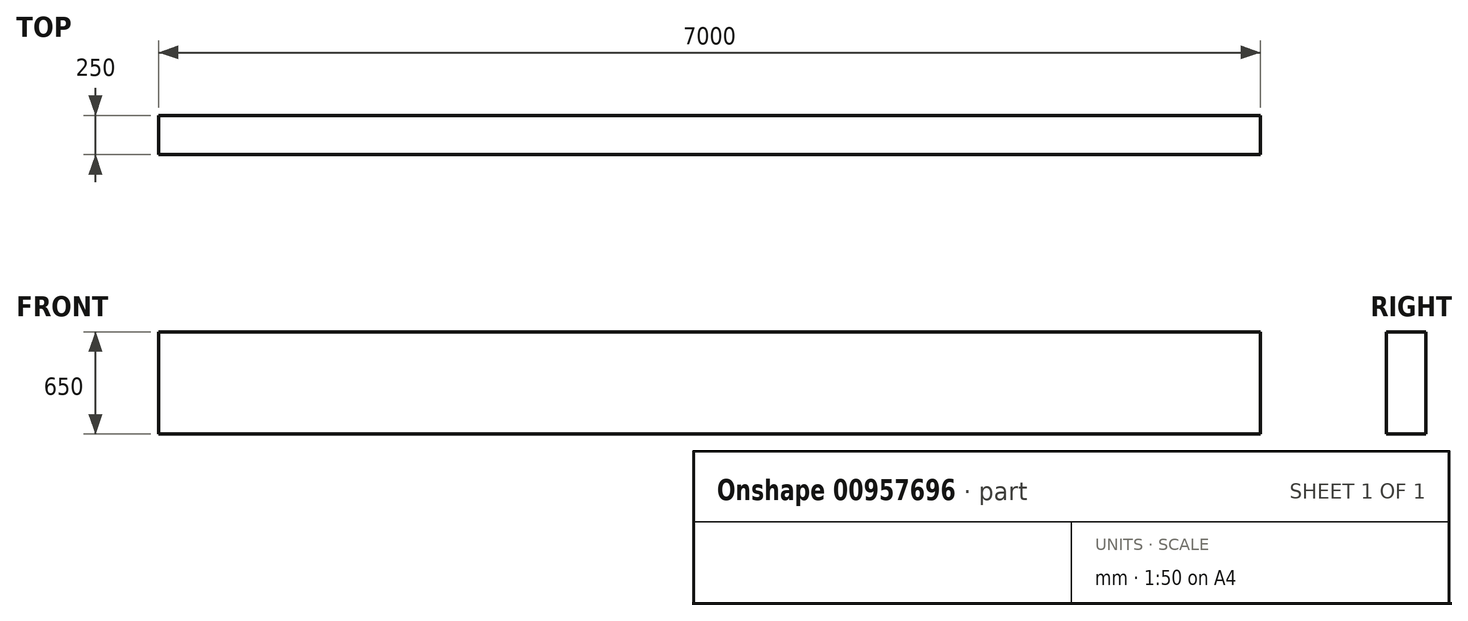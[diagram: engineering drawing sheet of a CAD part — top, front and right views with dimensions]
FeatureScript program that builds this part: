
annotation { "Feature Type Name" : "Feature", "Feature Type Description" : "" }
export const myFeature = defineFeature(function(context is Context, id is Id, definition is map)
    precondition{}
    {
        {
            var Q0;
            Q0=qCreatedBy(makeId("Front.planeOp"),FACE);
            var sketch = newSketch(context, id + "F0", { "sketchPlane" : qUnion([Q0])});
            skLineSegment(sketch, "E0", {"start": v(-3491.85, -4612.2) * mm, "end": v(3508.15, -4612.2) * mm});
            skLineSegment(sketch, "E1", {"start": v(3508.15, -4612.2) * mm, "end": v(3508.15, -5262.2) * mm});
            skLineSegment(sketch, "E2", {"start": v(3508.15, -5262.2) * mm, "end": v(-3491.85, -5262.2) * mm});
            skLineSegment(sketch, "E3", {"start": v(-3491.85, -5262.2) * mm, "end": v(-3491.85, -4612.2) * mm});
            skSolve(sketch);
        }
        {
            var Q0;
            Q0=makeQuery(id+"F0.imprint","IMPRINT",FACE,{"disambiguationData":[TD([[makeQuery(id+"F0.imprint","IMPRINT",EDGE,{"derivedFrom":sQuery(id+"F0.wireOp",EDGE,"E0")}),-1.0]])]});
            extrude(context, id + "F1", {"entities" : qUnion([Q0]), "depth" : 250 * mm, "offsetDistance" : 25 * mm});
        }
    });
